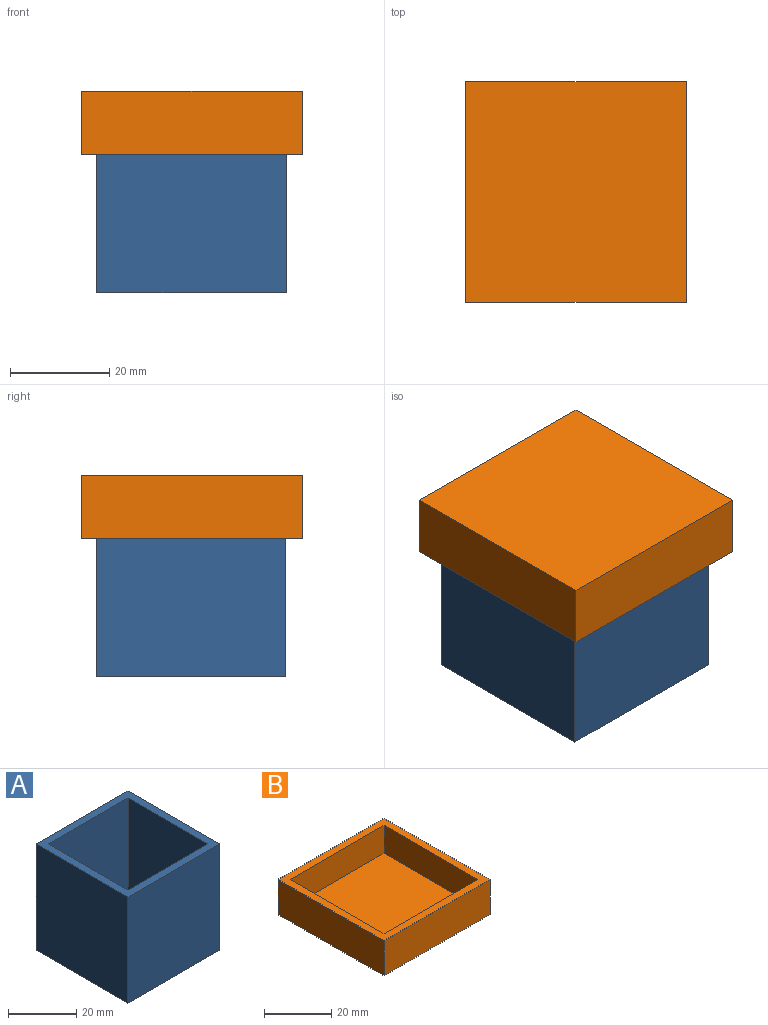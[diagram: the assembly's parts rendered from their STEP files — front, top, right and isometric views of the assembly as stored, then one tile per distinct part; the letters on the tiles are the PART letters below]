
ASSEMBLY  parts=2 mates=1
PART A: 11 faces, bbox 38.1x38.1x38.1 mm
  f0: plane 38.1x38.1mm, normal (0,0,1), area 361.3mm2, adj f1,f2,f3,f4,f6,f7,f8,f9
  f1: plane 38.1x38.1mm, normal (0,-1,0), area 1451.6mm2, adj f0,f2,f4,f5
  f2: plane 38.1x38.1mm, normal (1,0,0), area 1451.6mm2, adj f0,f1,f3,f5
  f3: plane 38.1x38.1mm, normal (0,1,0), area 1451.6mm2, adj f0,f2,f4,f5
  f4: plane 38.1x38.1mm, normal (-1,0,0), area 1451.6mm2, adj f0,f1,f3,f5
  f5: plane 38.1x38.1mm, normal (0,0,-1), area 1451.6mm2, adj f1,f2,f3,f4
  f6: plane 35.56x33.02mm, normal (0,1,0), area 1174.2mm2, adj f0,f7,f9,f10
  f7: plane 35.56x33.02mm, normal (-1,0,0), area 1174.2mm2, adj f0,f6,f8,f10
  f8: plane 35.56x33.02mm, normal (0,-1,0), area 1174.2mm2, adj f0,f7,f9,f10
  f9: plane 35.56x33.02mm, normal (1,0,0), area 1174.2mm2, adj f0,f6,f8,f10
  f10: plane 33.02x33.02mm, normal (0,0,1), area 1090.3mm2, adj f6,f7,f8,f9
PART B: 11 faces, bbox 44.5x44.5x12.7 mm
  f0: plane 44.45x12.7mm, normal (0,-1,0), area 564.5mm2, adj f1,f3,f4,f5
  f1: plane 44.45x12.7mm, normal (1,0,0), area 564.5mm2, adj f0,f2,f4,f5
  f2: plane 44.45x12.7mm, normal (0,1,0), area 564.5mm2, adj f1,f3,f4,f5
  f3: plane 44.45x12.7mm, normal (-1,0,0), area 564.5mm2, adj f0,f2,f4,f5
  f4: plane 44.45x44.45mm, normal (0,0,1), area 425.8mm2, adj f0,f1,f2,f3,f6,f7,f8,f9
  f5: plane 44.45x44.45mm, normal (0,0,-1), area 1975.8mm2, adj f0,f1,f2,f3
  f6: plane 39.37x10.16mm, normal (0,1,0), area 400mm2, adj f4,f7,f9,f10
  f7: plane 39.37x10.16mm, normal (-1,0,0), area 400mm2, adj f4,f6,f8,f10
  f8: plane 39.37x10.16mm, normal (0,-1,0), area 400mm2, adj f4,f7,f9,f10
  f9: plane 39.37x10.16mm, normal (1,0,0), area 400mm2, adj f4,f6,f8,f10
  f10: plane 39.37x39.37mm, normal (0,0,1), area 1550mm2, adj f6,f7,f8,f9
PLACE A t=(0,0,7.05)mm fixed
PLACE B rot(axis=(1,0,0),180deg) t=(0.09,37.88,85.79)mm
MATE planar B.f10 <-> A.f0  axis (0,0,-1) through (-38.64,-0.86,45.15)mm
